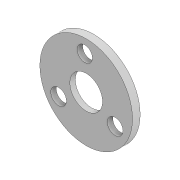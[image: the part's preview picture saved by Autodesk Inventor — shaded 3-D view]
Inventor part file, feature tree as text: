
AUTODESK INVENTOR PART (.ipt)
format: ipt  version: 2020.3 (Build 243373010, 373A)  size: 103,936 bytes
history: native  units: mm
features: extrude x2, sketch x2
ambient origin geometry x8: Origin, YZ Plane, XZ Plane, XY Plane, X Axis, Y Axis, Z Axis, Center Point
bodies: Solid1 (feature_tree)
feature tree (4):
  extrude  "Extrusion1"  Depth=3.5mm
  extrude  "Extrusion4"  Depth=1.0mm TaperAngle=0.0deg
  sketch  "Sketch1"  dims[d0=3.5mm d1=0.0mm d11=42.5mm]
  sketch  "Sketch3"  dims[d14=40.5mm d15=1.0mm d16=0.0mm]
